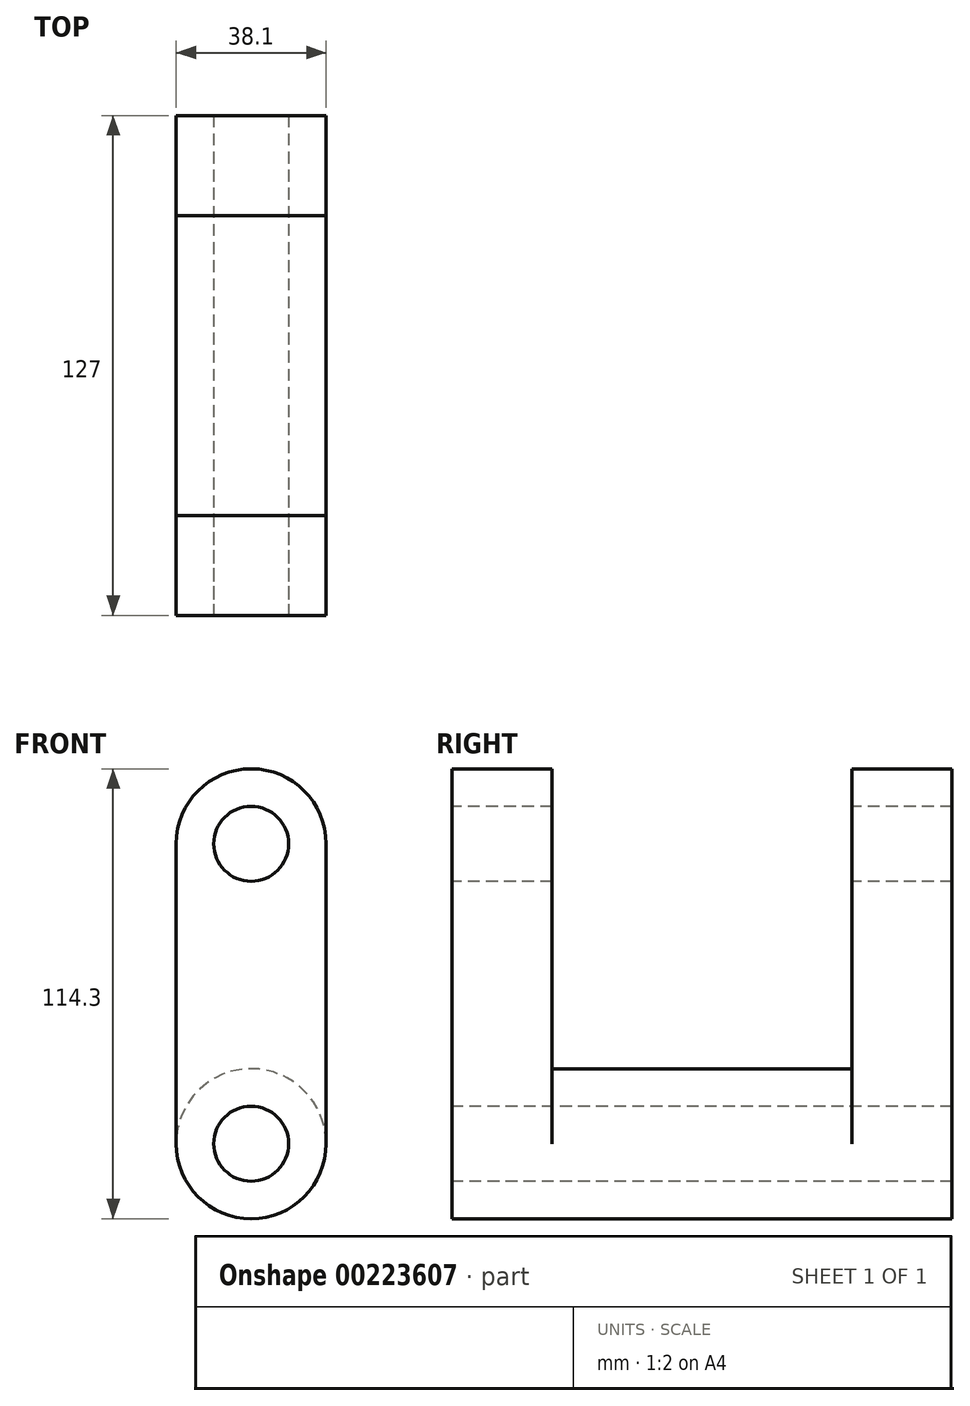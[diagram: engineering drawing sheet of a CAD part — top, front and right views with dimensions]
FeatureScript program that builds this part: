
annotation { "Feature Type Name" : "Feature", "Feature Type Description" : "" }
export const myFeature = defineFeature(function(context is Context, id is Id, definition is map)
    precondition{}
    {
        {
            var Q0;
            Q0=qCreatedBy(makeId("Front.planeOp"),FACE);
            var sketch = newSketch(context, id + "F0", { "sketchPlane" : qUnion([Q0])});
            skCircle(sketch, "E0", {"center": v(0, 0) * mm, "radius": 19.05 * mm});
            skSolve(sketch);
        }
        {
            var Q0;
            Q0=makeQuery(id+"F0.imprint","IMPRINT",FACE,{"disambiguationData":[TD([[makeQuery(id+"F0.imprint","IMPRINT",EDGE,{"derivedFrom":sQuery(id+"F0.wireOp",EDGE,"E0")}),1.0]])]});
            extrude(context, id + "F1", {"entities" : qUnion([Q0]), "endBound" : BoundingType.SYMMETRIC, "depth" : 76.2 * mm});
        }
        {
            var Q0;
            Q0=makeQuery(id+"F1.opExtrude","CAP_FACE",FACE,{"disambiguationData":[OSD([sQuery(id+"F0.wireOp",EDGE,"E0")])],"isStart":true});
            var sketch = newSketch(context, id + "F2", { "sketchPlane" : qUnion([Q0])});
            skCircle(sketch, "E1", {"center": v(0, 0) * mm, "radius": 19.05 * mm});
            skLineSegment(sketch, "E2.top", {"start": v(-19.05, 76.2) * mm, "end": v(19.05, 76.2) * mm});
            skLineSegment(sketch, "E2.left", {"start": v(-19.05, 0) * mm, "end": v(-19.05, 76.2) * mm});
            skLineSegment(sketch, "E2.right", {"start": v(19.05, 0) * mm, "end": v(19.05, 76.2) * mm});
            skArc(sketch, "E3", {"start": v(19.05, 76.2) * mm, "mid": v(0, 95.25) * mm, "end": v(-19.05, 76.2) * mm});
            skSolve(sketch);
        }
        {
            var Q0;
            Q0=makeQuery(id+"F2.imprint","IMPRINT",FACE,{"disambiguationData":[TD([[makeQuery(id+"F2.imprint","IMPRINT",EDGE,{"derivedFrom":sQuery(id+"F2.wireOp",EDGE,"E2.top")}),-1.0]])]});
            var Q1;
            Q1=makeQuery(id+"F2.imprint","IMPRINT",FACE,{"disambiguationData":[TD([[makeQuery(id+"F2.imprint","IMPRINT",EDGE,{"derivedFrom":sQuery(id+"F2.wireOp",EDGE,"E2.top")}),1.0]])]});
            var Q2;
            {var subQ0=sQuery(id+"F2.wireOp",EDGE,"E1");var subQ1=makeQuery(id+"F2.imprint","INTERSECT",VERTEX,{"derivedFrom":[subQ0,sQuery(id+"F2.wireOp",EDGE,"E2.left")]});Q2=makeQuery(id+"F2.imprint","IMPRINT",FACE,{"disambiguationData":[TD([[makeQuery(id+"F2.imprint","IMPRINT",EDGE,{"disambiguationData":[TD([[subQ1,-1.0]])],"derivedFrom":subQ0}),-1.0]])]});}
            extrude(context, id + "F3", {"entities" : qUnion([Q0, Q1, Q2]), "operationType" : NewBodyOperationType.ADD, "depth" : 25.4 * mm});
        }
        {
            var Q0;
            Q0=makeQuery(id+"F1.opExtrude","CAP_FACE",FACE,{"disambiguationData":[OSD([sQuery(id+"F0.wireOp",EDGE,"E0")])],"isStart":false});
            var sketch = newSketch(context, id + "F4", { "sketchPlane" : qUnion([Q0])});
            skCircle(sketch, "E4", {"center": v(0, 0) * mm, "radius": 19.05 * mm});
            skLineSegment(sketch, "E5.top", {"start": v(-19.05, 76.2) * mm, "end": v(19.05, 76.2) * mm});
            skLineSegment(sketch, "E5.left", {"start": v(-19.05, 0) * mm, "end": v(-19.05, 76.2) * mm});
            skLineSegment(sketch, "E5.right", {"start": v(19.05, 0) * mm, "end": v(19.05, 76.2) * mm});
            skArc(sketch, "E6", {"start": v(19.05, 76.2) * mm, "mid": v(0, 95.25) * mm, "end": v(-19.05, 76.2) * mm});
            skSolve(sketch);
        }
        {
            var Q0;
            Q0=makeQuery(id+"F4.imprint","IMPRINT",FACE,{"disambiguationData":[TD([[makeQuery(id+"F4.imprint","IMPRINT",EDGE,{"derivedFrom":sQuery(id+"F4.wireOp",EDGE,"E5.top")}),1.0]])]});
            var Q1;
            Q1=makeQuery(id+"F4.imprint","IMPRINT",FACE,{"disambiguationData":[TD([[makeQuery(id+"F4.imprint","IMPRINT",EDGE,{"derivedFrom":sQuery(id+"F4.wireOp",EDGE,"E5.top")}),-1.0]])]});
            var Q2;
            {var subQ0=sQuery(id+"F4.wireOp",EDGE,"E4");var subQ1=makeQuery(id+"F4.imprint","INTERSECT",VERTEX,{"derivedFrom":[subQ0,sQuery(id+"F4.wireOp",EDGE,"E5.left")]});Q2=makeQuery(id+"F4.imprint","IMPRINT",FACE,{"disambiguationData":[TD([[makeQuery(id+"F4.imprint","IMPRINT",EDGE,{"disambiguationData":[TD([[subQ1,1.0]])],"derivedFrom":subQ0}),1.0]])]});}
            extrude(context, id + "F5", {"entities" : qUnion([Q0, Q1, Q2]), "operationType" : NewBodyOperationType.ADD, "depth" : 25.4 * mm});
        }
        {
            var Q0;
            Q0=makeQuery(id+"F5.opExtrude","CAP_FACE",FACE,{"disambiguationData":[OSD([sQuery(id+"F4.wireOp",EDGE,"E4"),sQuery(id+"F4.wireOp",EDGE,"E5.left"),sQuery(id+"F4.wireOp",EDGE,"E5.right"),sQuery(id+"F4.wireOp",EDGE,"E6")])],"isStart":false});
            var sketch = newSketch(context, id + "F6", { "sketchPlane" : qUnion([Q0])});
            skCircle(sketch, "E7", {"center": v(0, 0) * mm, "radius": 9.53 * mm});
            skCircle(sketch, "E8", {"center": v(0, 76.2) * mm, "radius": 9.53 * mm});
            skSolve(sketch);
        }
        {
            var Q0;
            Q0=makeQuery(id+"F6.imprint","IMPRINT",FACE,{"disambiguationData":[TD([[makeQuery(id+"F6.imprint","IMPRINT",EDGE,{"derivedFrom":sQuery(id+"F6.wireOp",EDGE,"E8")}),1.0]])]});
            var Q1;
            Q1=makeQuery(id+"F6.imprint","IMPRINT",FACE,{"disambiguationData":[TD([[makeQuery(id+"F6.imprint","IMPRINT",EDGE,{"derivedFrom":sQuery(id+"F6.wireOp",EDGE,"E7")}),1.0]])]});
            extrude(context, id + "F7", {"entities" : qUnion([Q0, Q1]), "operationType" : NewBodyOperationType.REMOVE, "oppositeDirection" : true, "depth" : 138.43 * mm});
        }
    });
